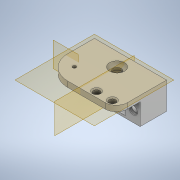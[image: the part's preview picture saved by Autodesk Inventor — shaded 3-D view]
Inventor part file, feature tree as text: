
AUTODESK INVENTOR PART (.ipt)
format: ipt  version: 2021 (Build 250183000, 183)  size: 647,680 bytes
history: native  units: in
note: dims shown in document units (in); Inventor stores cm internally (conversion verified against a paired STEP export)
features: extrude x11, sketch x10, projected_geometry x10, fillet x5, plane x4, chamfer x4, mirror x1
ambient origin geometry x8: Origin, YZ Plane, XZ Plane, XY Plane, X Axis, Y Axis, Z Axis, Center Point
bodies: Solid1 (feature_tree)
feature tree (45):
  plane  "Work Plane1"
  extrude  "Extrusion1"  Depth=0.1969in TaperAngle=0.0deg
  fillet  "Fillet1"  Radius=0.1181in
  extrude  "Extrusion2"  Depth=0.0787in TaperAngle=0.0deg
  extrude  "Extrusion3"  Depth=0.0787in
  extrude  "Extrusion4"  Depth=0.5906in TaperAngle=0.0deg
  extrude  "Extrusion5"  Depth=0.3937in TaperAngle=0.0deg
  extrude  "Extrusion6"  Depth=0.3012in
  extrude  "Extrusion7"  Depth=0.3937in TaperAngle=0.0deg
  extrude  "Extrusion8"  TaperAngle=0.0deg  [1 undecoded]
  plane  "Work Plane2"
  extrude  "Extrusion11"  Depth=0.2224in
  extrude  "Extrusion12"  TaperAngle=0.0deg  [1 undecoded]
  chamfer  "Chamfer4"  Distance=0.0394in Angle=45.0deg
  chamfer  "Chamfer5"  Distance=0.0394in Angle=45.0deg
  fillet  "Fillet2"  Radius=0.8268in
  fillet  "Fillet3"  Radius=0.3937in
  plane  "Work Plane4"
  plane  "Work Plane3"
  extrude  "Extrusion17"  TaperAngle=0.0deg  [1 undecoded]
  chamfer  "Chamfer8"  Distance=0.4331in
  chamfer  "Chamfer9"  Distance=0.25in
  fillet  "Fillet4"  Radius=0.2756in
  mirror  "Mirror4"
  fillet  "Fillet5"  Radius=0.0787in
  sketch  "Sketch1"  dims[d0=-0.2756in d1=0.1969in d2=0.0in d3=0.1181in]
  projected_geometry  "Projected Loop1"
  sketch  "Sketch2"  dims[d4=1.1811in d6=0.0787in d7=0.0in]
  projected_geometry  "Projected Loop2"
  sketch  "Sketch3"  dims[d8=0.0787in d9=0.0787in]
  projected_geometry  "Projected Loop3"
  sketch  "Sketch4"  dims[d10=0.5906in d11=0.0in d12=0.0787in d13=0.0in]
  sketch  "Sketch5"  dims[d14=0.3937in d15=0.0in d16=0.3937in d17=0.0in]
  projected_geometry  "Projected Loop4"
  projected_geometry  "Projected Loop5"
  sketch  "Sketch6"  dims[d18=0.8795in d19=0.3012in]
  projected_geometry  "Projected Loop6"
  sketch  "Sketch7"  dims[d22=0.3937in d23=0.0in d28=0.0591in d29=0.0in]
  projected_geometry  "Projected Loop7"
  sketch  "Sketch8"  dims[d48=0.1969in d49=0.0in d50=0.0in]
  sketch  "Sketch13"  dims[d51=1.1811in d53=0.2224in]
  projected_geometry  "Projected Loop11"
  sketch  "Sketch17"  dims[d54=0.2224in d55=0.0in d56=0.0in d57=0.0394in d58=0.0787in d59=45.0deg d60=0.0394in d61=0.0787in d62=45.0deg d63=0.8268in d64=0.3937in d81=0.0in d85=0.4331in d86=0.25in d87=0.2756in d88=0.0787in d89=0.0in d90=0.1575in d91=0.0787in d92=45.0deg d93=0.0197in d94=0.0787in d95=45.0deg d96=0.315in d97=0.5906in d5=1.9685in d39=0.0197in d40=1.9685in d41=0.0197in d42=1.9685in]
  projected_geometry  "Projected Loop16"
  projected_geometry  "Projected Loop17"
note: 3 required parameter values undecoded (feature->parameter linkage not recoverable at this tier; creation-order binding heuristic only, values carry confidence <= 0.55)
